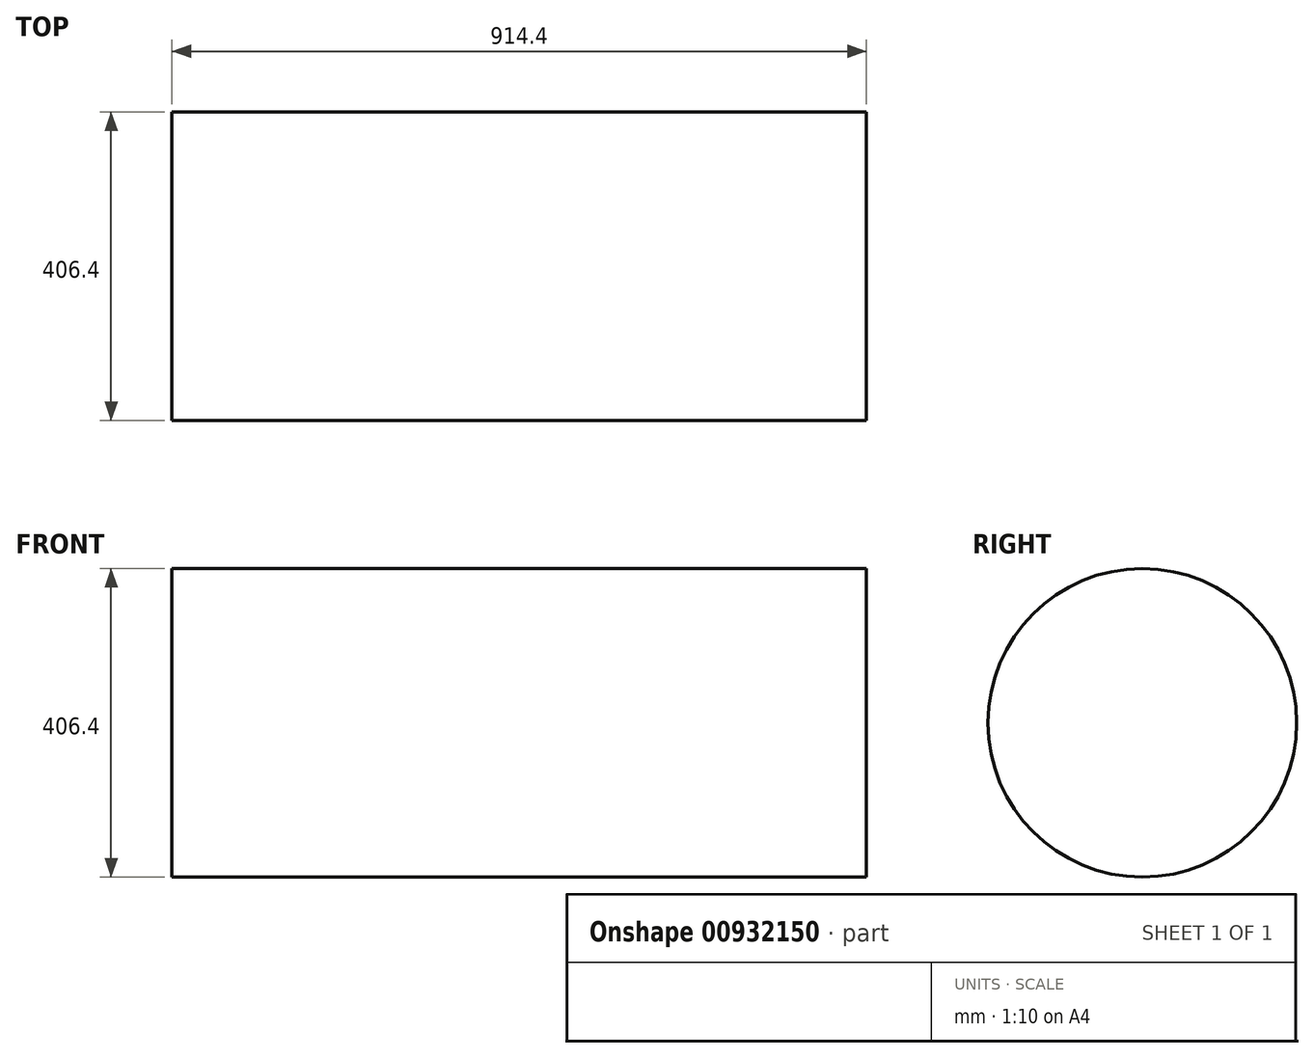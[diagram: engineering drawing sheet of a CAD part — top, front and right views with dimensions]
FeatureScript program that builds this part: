
annotation { "Feature Type Name" : "Feature", "Feature Type Description" : "" }
export const myFeature = defineFeature(function(context is Context, id is Id, definition is map)
    precondition{}
    {
        {
            var Q0;
            Q0=qCreatedBy(makeId("Right.planeOp"),FACE);
            var sketch = newSketch(context, id + "F0", { "sketchPlane" : qUnion([Q0])});
            skCircle(sketch, "E0", {"center": v(0, 0) * mm, "radius": 203.2 * mm});
            skSolve(sketch);
        }
        {
            var Q0;
            Q0 = qSketchRegion(id + "F0", true);
            extrude(context, id + "F1", {"entities" : qUnion([Q0]), "endBound" : BoundingType.SYMMETRIC, "depth" : 914.4 * mm, "offsetDistance" : 25.4 * mm});
        }
    });
